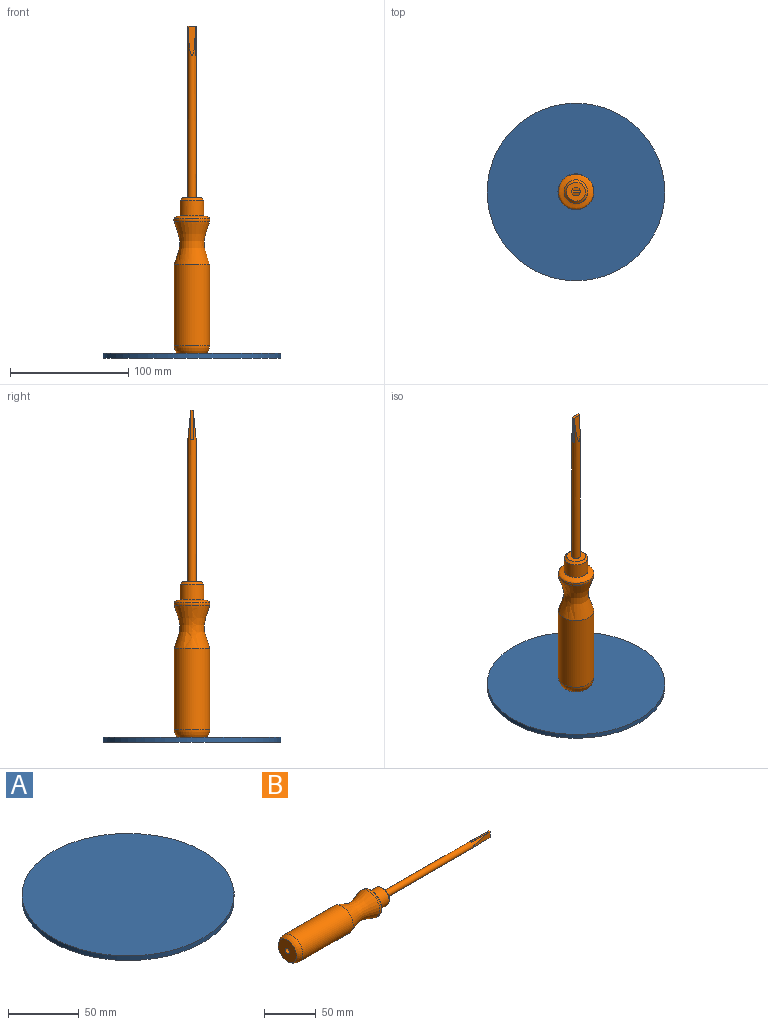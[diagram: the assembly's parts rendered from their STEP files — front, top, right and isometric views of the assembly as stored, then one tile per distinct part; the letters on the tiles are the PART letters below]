
ASSEMBLY  parts=2 mates=1
PART A: 3 faces, bbox 150x150x4 mm
  f0: cylinder r=75mm len=150mm, axis (0,0,-1), area 1885mm2, adj f1,f2
  f1: plane 150x150mm, normal (0,0,1), area 17671.5mm2, adj f0
  f2: plane 150x150mm, normal (0,0,-1), area 17671.5mm2, adj f0
PART B: 25 faces, bbox 276.4x30.3x30.3 mm
  f0: plane 25x0.15mm, normal (0,1,0), area 3.6mm2, adj f2,f11,f16,f18
  f1: plane 25x0.15mm, normal (0,-1,0), area 3.6mm2, adj f2,f12,f16,f18
  f2: cylinder r=3.5mm len=145mm, axis (-1,0,0), area 2797.1mm2, adj f0,f1,f3,f11,f12,f13,f15,f17
  f3: plane 16x16mm, normal (1,0,0), area 162.6mm2, adj f2,f10
  f4: cylinder r=10mm len=20mm, axis (-1,0,0), area 816.8mm2, adj f5,f10
  f5: revolved ~30x30mm, area 460.1mm2, adj f4,f6
  f6: revolved ~30.31x30.31mm, area 228.2mm2, adj f5,f7
  f7: revolved ~36.32x30mm, area 2880.9mm2, adj f6,f8
  f8: cylinder r=15mm len=68.77mm, axis (-1,0,0), area 6481.6mm2, adj f7,f9
  f9: torus R=5mm, axis (-1,0,0), area 619mm2, adj f8,f22
  f10: cone r=10mm half-angle=45deg, axis (-1,0,0), area 159.9mm2, adj f3,f4
  f11: plane 1x0.15mm, normal (-1,0,0), area 0mm2, adj f0,f2,f16
  f12: plane 1x0.15mm, normal (-1,0,0), area 0mm2, adj f1,f2,f16
  f13: plane 1x0.15mm, normal (-1,0,0), area 0mm2, adj f2,f14,f17
  f14: plane 25x2mm, normal (0,0,1), area 50mm2, adj f13,f15,f17,f18,f19
  f15: plane 25x0.15mm, normal (0,-1,0), area 3.6mm2, adj f2,f14,f18,f19
  f16: plane 25x2mm, normal (0,0,-1), area 50mm2, adj f0,f1,f11,f12,f18
  f17: plane 25x0.15mm, normal (0,1,0), area 3.6mm2, adj f2,f13,f14,f18
  f18: plane 7x2mm, normal (1,0,0), area 14mm2, adj f0,f1,f14,f15,f16,f17,f20,f21
  f19: plane 1x0.15mm, normal (-1,0,0), area 0mm2, adj f2,f14,f15
  f20: plane 25x6.71mm, normal (0.1,-1,0), area 124mm2, adj f2,f18
  f21: plane 25x6.71mm, normal (0.1,1,0), area 124mm2, adj f2,f18
  f22: plane 25.39x25.39mm, normal (-1,0,0), area 478mm2, adj f9,f23
  f23: cylinder r=3mm len=12.5mm, axis (-1,0,0), area 235.6mm2, adj f22,f24
  f24: plane 6x6mm, normal (-1,0,0), area 28.3mm2, adj f23
PLACE A t=(-47.71,-4.07,-23.94)mm
PLACE B rot(axis=(0,-1,0),90deg) t=(-47.71,-4.07,105.06)mm
MATE planar B.f2 <-> A.f0  axis (0,0,-1) through (-47.71,-4.07,-19.94)mm
